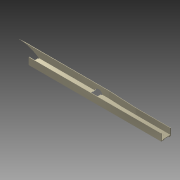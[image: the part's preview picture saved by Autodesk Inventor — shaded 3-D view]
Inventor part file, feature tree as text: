
AUTODESK INVENTOR PART (.ipt)
format: ipt  version: 2015 (Build 190159000, 159)  size: 162,304 bytes
history: native  units: mm
features: extrude x5, sketch x5, shell x1, pattern_linear x1, fillet x1
ambient origin geometry x8: Origin, YZ Plane, XZ Plane, XY Plane, X Axis, Y Axis, Z Axis, Center Point
bodies: 实体1 (feature_tree)
feature tree (13):
  extrude  "拉伸1"  Depth=80.0mm
  extrude  "拉伸2"  Depth=10.0mm
  shell  "抽壳1"  Thickness=10.0mm
  extrude  "拉伸3"  Depth=20.0mm
  pattern_linear  "矩形阵列1"  Count1=2  [1 undecoded]
  extrude  "拉伸4"  Depth=5.0mm
  extrude  "拉伸5"  Depth=3.0mm TaperAngle=0.0deg
  fillet  "圆角1"  Radius=3.0mm
  sketch  "草图1"  dims[d0=950.0mm d1=80.0mm]
  sketch  "草图2"  dims[d2=250.0mm d3=200.0mm d4=10.0mm]
  sketch  "草图3"  dims[d5=50.0mm d6=0.0mm d7=20.0mm d8=20.0mm]
  sketch  "草图4"  dims[d9=30.0mm d10=5.0mm]
  sketch  "草图5"  dims[d11=135.0deg d12=950.0mm d13=0.0mm d14=3.0mm d15=5.0mm d16=25.0mm d17=40.0mm d18=3.0mm d19=0.0mm d20=100.0mm d22=100.0mm d23=25.0mm d24=525.0mm d25=120.0deg d26=45.0mm d27=0.0mm d28=150.0mm d29=3.0mm d30=0.0mm d31=3.0mm]
note: 1 required parameter value undecoded (feature->parameter linkage not recoverable at this tier; creation-order binding heuristic only, values carry confidence <= 0.55)
